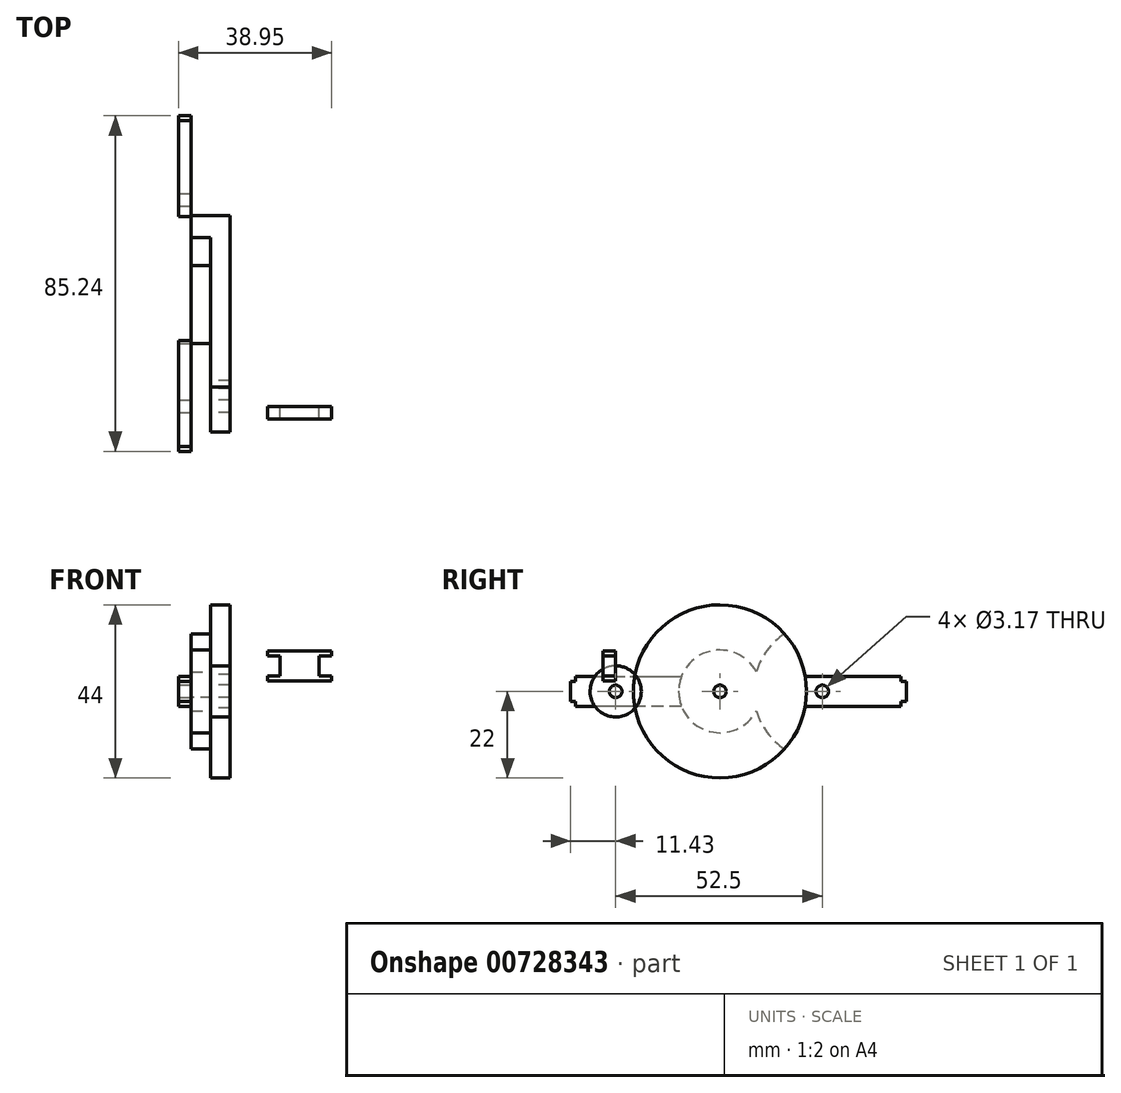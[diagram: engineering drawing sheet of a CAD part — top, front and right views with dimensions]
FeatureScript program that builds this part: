
annotation { "Feature Type Name" : "Feature", "Feature Type Description" : "" }
export const myFeature = defineFeature(function(context is Context, id is Id, definition is map)
    precondition{}
    {
        {
            var Q0;
            Q0=qCreatedBy(makeId("Right.planeOp"),FACE);
            var sketch = newSketch(context, id + "F0", { "sketchPlane" : qUnion([Q0])});
            skCircle(sketch, "E0", {"center": v(0, 0) * mm, "radius": 6.5 * mm});
            skCircle(sketch, "E1", {"center": v(0, 0) * mm, "radius": 4.5 * mm});
            skLineSegment(sketch, "E2", {"start": v(0, 0) * mm, "end": v(26.5, 0) * mm});
            skCircle(sketch, "E3", {"center": v(26.5, 0) * mm, "radius": 20 * mm});
            skCircle(sketch, "E4", {"center": v(26.5, 0) * mm, "radius": 22 * mm});
            skLineSegment(sketch, "E5.bottom", {"start": v(48.5, -25.09) * mm, "end": v(-11.83, -25.09) * mm});
            skLineSegment(sketch, "E5.top", {"start": v(48.5, 25.71) * mm, "end": v(-11.83, 25.71) * mm});
            skLineSegment(sketch, "E5.left", {"start": v(48.5, -25.09) * mm, "end": v(48.5, 25.71) * mm});
            skLineSegment(sketch, "E5.right", {"start": v(-11.83, -25.09) * mm, "end": v(-11.83, 25.71) * mm});
            skPoint(sketch, "E6", {"position": v(48.5, 0.31) * mm});
            skCircle(sketch, "E7", {"center": v(26.5, 0) * mm, "radius": 1.59 * mm});
            skCircle(sketch, "E8", {"center": v(0, 0) * mm, "radius": 1.59 * mm});
            skLineSegment(sketch, "E9.bottom", {"start": v(48.5, 25.71) * mm, "end": v(51.67, 25.71) * mm});
            skLineSegment(sketch, "E9.top", {"start": v(48.5, -25.09) * mm, "end": v(51.67, -25.09) * mm});
            skLineSegment(sketch, "E9.left", {"start": v(48.5, 25.71) * mm, "end": v(48.5, -25.09) * mm});
            skLineSegment(sketch, "E9.right", {"start": v(51.67, 25.71) * mm, "end": v(51.67, -25.09) * mm});
            skSolve(sketch);
        }
        {
            var Q0;
            Q0=makeQuery(id+"F0.imprint","IMPRINT",FACE,{"disambiguationData":[TD([[makeQuery(id+"F0.imprint","IMPRINT",EDGE,{"derivedFrom":sQuery(id+"F0.wireOp",EDGE,"E1")}),1.0]])]});
            var Q1;
            Q1=makeQuery(id+"F0.imprint","IMPRINT",FACE,{"disambiguationData":[TD([[makeQuery(id+"F0.imprint","IMPRINT",EDGE,{"derivedFrom":sQuery(id+"F0.wireOp",EDGE,"E3")}),1.0]])]});
            var Q2;
            {var subQ0=sQuery(id+"F0.wireOp",EDGE,"E4");var subQ1=sQuery(id+"F0.wireOp",EDGE,"E0");var subQ2=makeQuery(id+"F0.imprint","INTERSECT",VERTEX,{"disambiguationData":[OD(0.0)],"derivedFrom":[subQ1,subQ0]});Q2=makeQuery(id+"F0.imprint","IMPRINT",FACE,{"disambiguationData":[TD([[makeQuery(id+"F0.imprint","IMPRINT",EDGE,{"disambiguationData":[TD([[subQ2,1.0]])],"derivedFrom":subQ1}),1.0]])]});}
            var Q3;
            {var subQ1=sQuery(id+"F0.wireOp",EDGE,"E0");var subQ3=sQuery(id+"F0.wireOp",EDGE,"E4");var subQ4=makeQuery(id+"F0.imprint","INTERSECT",VERTEX,{"disambiguationData":[OD(1.0)],"derivedFrom":[subQ1,subQ3]});Q3=makeQuery(id+"F0.imprint","IMPRINT",FACE,{"disambiguationData":[TD([[makeQuery(id+"F0.imprint","IMPRINT",EDGE,{"disambiguationData":[TD([[subQ4,-1.0]])],"derivedFrom":subQ1}),1.0]])]});}
            var Q4;
            {var subQ4=sQuery(id+"F0.wireOp",EDGE,"E3");Q4=makeQuery(id+"F0.imprint","IMPRINT",FACE,{"disambiguationData":[TD([[makeQuery(id+"F0.imprint","IMPRINT",EDGE,{"derivedFrom":subQ4}),-1.0]])]});}
            var Q5;
            {var subQ4=sQuery(id+"F0.wireOp",EDGE,"E1");Q5=makeQuery(id+"F0.imprint","IMPRINT",FACE,{"disambiguationData":[TD([[makeQuery(id+"F0.imprint","IMPRINT",EDGE,{"derivedFrom":subQ4}),-1.0]])]});}
            extrude(context, id + "F1", {"entities" : qUnion([Q0, Q1, Q2, Q3, Q4, Q5]), "depth" : 5 * mm, "offsetDistance" : 25.4 * mm});
        }
        {
            var Q0;
            Q0=makeQuery(id+"F1.opExtrude","CAP_FACE",FACE,{"disambiguationData":[OSD([sQuery(id+"F0.wireOp",EDGE,"E0"),sQuery(id+"F0.wireOp",EDGE,"E4"),sQuery(id+"F0.wireOp",EDGE,"E7"),sQuery(id+"F0.wireOp",EDGE,"E8")])],"isStart":true});
            var sketch = newSketch(context, id + "F2", { "sketchPlane" : qUnion([Q0])});
            skCircle(sketch, "E10", {"center": v(-26.5, 0) * mm, "radius": 8.5 * mm});
            skCircle(sketch, "E11", {"center": v(-26.5, 0) * mm, "radius": 10.5 * mm});
            skLineSegment(sketch, "E12", {"start": v(-26.5, 0) * mm, "end": v(-52.5, 0) * mm});
            skCircle(sketch, "E13", {"center": v(-52.5, 0) * mm, "radius": 17.5 * mm});
            skCircle(sketch, "E14", {"center": v(-52.5, 0) * mm, "radius": 15.5 * mm});
            skCircle(sketch, "E15", {"center": v(-52.5, 0) * mm, "radius": 1.59 * mm});
            skSolve(sketch);
        }
        {
            var Q0;
            {var subQ1=sQuery(id+"F2.wireOp",EDGE,"E12");var subQ3=makeQuery(id+"F1.opExtrude","CAP_EDGE",EDGE,{"disambiguationData":[OSD([sQuery(id+"F0.wireOp",EDGE,"E4")])],"isStart":true});var subQ4=makeQuery(id+"F2.imprint","INTERSECT",VERTEX,{"derivedFrom":[subQ3,subQ1]});Q0=makeQuery(id+"F2.imprint","IMPRINT",FACE,{"disambiguationData":[TD([[makeQuery(id+"F2.imprint","IMPRINT",EDGE,{"disambiguationData":[TD([[subQ4,1.0]])],"derivedFrom":subQ3}),-1.0]])]});}
            var Q1;
            {var subQ1=sQuery(id+"F2.wireOp",EDGE,"E12");var subQ3=makeQuery(id+"F1.opExtrude","CAP_EDGE",EDGE,{"disambiguationData":[OSD([sQuery(id+"F0.wireOp",EDGE,"E4")])],"isStart":true});var subQ4=makeQuery(id+"F2.imprint","INTERSECT",VERTEX,{"derivedFrom":[subQ3,subQ1]});Q1=makeQuery(id+"F2.imprint","IMPRINT",FACE,{"disambiguationData":[TD([[makeQuery(id+"F2.imprint","IMPRINT",EDGE,{"disambiguationData":[TD([[subQ4,-1.0]])],"derivedFrom":subQ3}),-1.0]])]});}
            var Q2;
            {var subQ0=sQuery(id+"F2.wireOp",EDGE,"E14");var subQ1=makeQuery(id+"F1.opExtrude","CAP_EDGE",EDGE,{"disambiguationData":[OSD([sQuery(id+"F0.wireOp",EDGE,"E4")])],"isStart":true});var subQ2=makeQuery(id+"F2.imprint","INTERSECT",VERTEX,{"disambiguationData":[OD(0.0)],"derivedFrom":[subQ1,subQ0]});Q2=makeQuery(id+"F2.imprint","IMPRINT",FACE,{"disambiguationData":[TD([[makeQuery(id+"F2.imprint","IMPRINT",EDGE,{"disambiguationData":[TD([[subQ2,-1.0]])],"derivedFrom":subQ0}),1.0]])]});}
            var Q3;
            Q3=makeQuery(id+"F2.imprint","IMPRINT",FACE,{"disambiguationData":[TD([[makeQuery(id+"F2.imprint","IMPRINT",EDGE,{"derivedFrom":sQuery(id+"F2.wireOp",EDGE,"E10")}),1.0]])]});
            var Q4;
            {var subQ0=sQuery(id+"F2.wireOp",EDGE,"E13");var subQ1=sQuery(id+"F2.wireOp",EDGE,"E11");var subQ2=makeQuery(id+"F2.imprint","INTERSECT",VERTEX,{"disambiguationData":[OD(0.0)],"derivedFrom":[subQ1,subQ0]});Q4=makeQuery(id+"F2.imprint","IMPRINT",FACE,{"disambiguationData":[TD([[makeQuery(id+"F2.imprint","IMPRINT",EDGE,{"disambiguationData":[TD([[subQ2,-1.0]])],"derivedFrom":subQ1}),1.0]])]});}
            var Q5;
            {var subQ0=sQuery(id+"F2.wireOp",EDGE,"E13");var subQ1=sQuery(id+"F2.wireOp",EDGE,"E11");var subQ2=makeQuery(id+"F2.imprint","INTERSECT",VERTEX,{"disambiguationData":[OD(1.0)],"derivedFrom":[subQ1,subQ0]});Q5=makeQuery(id+"F2.imprint","IMPRINT",FACE,{"disambiguationData":[TD([[makeQuery(id+"F2.imprint","IMPRINT",EDGE,{"disambiguationData":[TD([[subQ2,1.0]])],"derivedFrom":subQ1}),1.0]])]});}
            var Q6;
            {var subQ0=sQuery(id+"F2.wireOp",EDGE,"E13");var subQ1=sQuery(id+"F2.wireOp",EDGE,"E11");var subQ2=makeQuery(id+"F2.imprint","INTERSECT",VERTEX,{"disambiguationData":[OD(1.0)],"derivedFrom":[subQ1,subQ0]});Q6=makeQuery(id+"F2.imprint","IMPRINT",FACE,{"disambiguationData":[TD([[makeQuery(id+"F2.imprint","IMPRINT",EDGE,{"disambiguationData":[TD([[subQ2,1.0]])],"derivedFrom":subQ0}),1.0]])]});}
            var Q7;
            {var subQ0=sQuery(id+"F2.wireOp",EDGE,"E10");Q7=makeQuery(id+"F2.imprint","IMPRINT",FACE,{"disambiguationData":[TD([[makeQuery(id+"F2.imprint","IMPRINT",EDGE,{"derivedFrom":subQ0}),-1.0]])]});}
            var Q8;
            {var subQ0=sQuery(id+"F2.wireOp",EDGE,"E13");var subQ1=sQuery(id+"F2.wireOp",EDGE,"E11");var subQ2=makeQuery(id+"F2.imprint","INTERSECT",VERTEX,{"disambiguationData":[OD(0.0)],"derivedFrom":[subQ1,subQ0]});Q8=makeQuery(id+"F2.imprint","IMPRINT",FACE,{"disambiguationData":[TD([[makeQuery(id+"F2.imprint","IMPRINT",EDGE,{"disambiguationData":[TD([[subQ2,-1.0]])],"derivedFrom":subQ0}),1.0]])]});}
            var Q9;
            {var subQ0=sQuery(id+"F2.wireOp",EDGE,"E13");var subQ1=makeQuery(id+"F1.opExtrude","CAP_EDGE",EDGE,{"disambiguationData":[OSD([sQuery(id+"F0.wireOp",EDGE,"E4")])],"isStart":true});var subQ2=makeQuery(id+"F2.imprint","INTERSECT",VERTEX,{"disambiguationData":[OD(0.0)],"derivedFrom":[subQ1,subQ0]});Q9=makeQuery(id+"F2.imprint","IMPRINT",FACE,{"disambiguationData":[TD([[makeQuery(id+"F2.imprint","IMPRINT",EDGE,{"disambiguationData":[TD([[subQ2,-1.0]])],"derivedFrom":subQ0}),1.0]])]});}
            extrude(context, id + "F3", {"entities" : qUnion([Q0, Q1, Q2, Q3, Q4, Q5, Q6, Q7, Q8, Q9]), "operationType" : NewBodyOperationType.ADD, "depth" : 5 * mm, "offsetDistance" : 25.4 * mm});
        }
        {
            var Q0;
            Q0=makeQuery(id+"F3.opExtrude","CAP_FACE",FACE,{"disambiguationData":[OSD([sQuery(id+"F0.wireOp",EDGE,"E7"),sQuery(id+"F2.wireOp",EDGE,"E11"),sQuery(id+"F2.wireOp",EDGE,"E13"),sQuery(id+"F2.wireOp",EDGE,"E15")])],"isStart":false});
            var sketch = newSketch(context, id + "F4", { "sketchPlane" : qUnion([Q0])});
            skCircle(sketch, "E16", {"center": v(-52.5, 0) * mm, "radius": 1.59 * mm});
            skCircle(sketch, "E17", {"center": v(-26.5, 0) * mm, "radius": 1.59 * mm});
            skLineSegment(sketch, "E18", {"start": v(-52.5, 0) * mm, "end": v(-70, 0) * mm});
            skLineSegment(sketch, "E19", {"start": v(-70, 0) * mm, "end": v(-72.54, 0) * mm});
            skLineSegment(sketch, "E20", {"start": v(-72.54, 0) * mm, "end": v(-72.54, -3.81) * mm});
            skLineSegment(sketch, "E21", {"start": v(-72.54, -3.81) * mm, "end": v(0, -3.81) * mm});
            skLineSegment(sketch, "E22", {"start": v(0, -3.81) * mm, "end": v(10.16, -3.81) * mm});
            skLineSegment(sketch, "E23", {"start": v(10.16, -3.8) * mm, "end": v(10.16, 0) * mm});
            skLineSegment(sketch, "E24", {"start": v(10.16, 0) * mm, "end": v(10.16, 3.81) * mm});
            skLineSegment(sketch, "E25", {"start": v(10.16, 3.81) * mm, "end": v(-72.54, 3.81) * mm});
            skLineSegment(sketch, "E26", {"start": v(-72.54, 3.81) * mm, "end": v(-72.54, 0) * mm});
            skLineSegment(sketch, "E27", {"start": v(-72.54, 0) * mm, "end": v(-73.8, 0) * mm});
            skLineSegment(sketch, "E28", {"start": v(-73.8, 0) * mm, "end": v(-73.8, -2.54) * mm});
            skLineSegment(sketch, "E29", {"start": v(-73.8, -2.54) * mm, "end": v(-72.54, -2.54) * mm});
            skLineSegment(sketch, "E30.MirrorCS", {"start": v(-73.8, 0) * mm, "end": v(-73.8, 2.54) * mm});
            skLineSegment(sketch, "E31.MirrorCS", {"start": v(-73.8, 2.54) * mm, "end": v(-72.54, 2.54) * mm});
            skLineSegment(sketch, "E32", {"start": v(10.16, 0) * mm, "end": v(11.43, 0) * mm});
            skLineSegment(sketch, "E33", {"start": v(11.43, 0) * mm, "end": v(11.43, -2.54) * mm});
            skLineSegment(sketch, "E34", {"start": v(11.43, -2.54) * mm, "end": v(10.16, -2.54) * mm});
            skLineSegment(sketch, "E35.MirrorCS", {"start": v(11.43, 0) * mm, "end": v(11.43, 2.54) * mm});
            skLineSegment(sketch, "E36.MirrorCS", {"start": v(11.43, 2.54) * mm, "end": v(10.16, 2.54) * mm});
            skCircle(sketch, "E37", {"center": v(0, 0) * mm, "radius": 1.59 * mm});
            skSolve(sketch);
        }
        {
            var Q0;
            Q0=makeQuery(id+"F4.imprint","IMPRINT",FACE,{"disambiguationData":[TD([[makeQuery(id+"F4.imprint","IMPRINT",EDGE,{"derivedFrom":sQuery(id+"F4.wireOp",EDGE,"E16")}),-1.0]])]});
            var Q1;
            {var subQ6=sQuery(id+"F4.wireOp",EDGE,"E19");Q1=makeQuery(id+"F4.imprint","IMPRINT",FACE,{"disambiguationData":[TD([[makeQuery(id+"F4.imprint","IMPRINT",EDGE,{"derivedFrom":subQ6}),-1.0]])]});}
            var Q2;
            {var subQ6=sQuery(id+"F4.wireOp",EDGE,"E19");Q2=makeQuery(id+"F4.imprint","IMPRINT",FACE,{"disambiguationData":[TD([[makeQuery(id+"F4.imprint","IMPRINT",EDGE,{"derivedFrom":subQ6}),1.0]])]});}
            var Q3;
            {var subQ0=sQuery(id+"F4.wireOp",EDGE,"E27");Q3=makeQuery(id+"F4.imprint","IMPRINT",FACE,{"disambiguationData":[TD([[makeQuery(id+"F4.imprint","IMPRINT",EDGE,{"derivedFrom":subQ0}),1.0]])]});}
            var Q4;
            {var subQ0=sQuery(id+"F4.wireOp",EDGE,"E27");Q4=makeQuery(id+"F4.imprint","IMPRINT",FACE,{"disambiguationData":[TD([[makeQuery(id+"F4.imprint","IMPRINT",EDGE,{"derivedFrom":subQ0}),-1.0]])]});}
            var Q5;
            {var subQ4=sQuery(id+"F4.wireOp",EDGE,"E22");Q5=makeQuery(id+"F4.imprint","IMPRINT",FACE,{"disambiguationData":[TD([[makeQuery(id+"F4.imprint","IMPRINT",EDGE,{"derivedFrom":subQ4}),1.0]])]});}
            var Q6;
            {var subQ0=sQuery(id+"F4.wireOp",EDGE,"E32");Q6=makeQuery(id+"F4.imprint","IMPRINT",FACE,{"disambiguationData":[TD([[makeQuery(id+"F4.imprint","IMPRINT",EDGE,{"derivedFrom":subQ0}),1.0]])]});}
            var Q7;
            {var subQ0=sQuery(id+"F4.wireOp",EDGE,"E32");Q7=makeQuery(id+"F4.imprint","IMPRINT",FACE,{"disambiguationData":[TD([[makeQuery(id+"F4.imprint","IMPRINT",EDGE,{"derivedFrom":subQ0}),-1.0]])]});}
            extrude(context, id + "F5", {"entities" : qUnion([Q0, Q1, Q2, Q3, Q4, Q5, Q6, Q7]), "depth" : 3.17 * mm, "offsetDistance" : 25.4 * mm});
        }
        {
            var Q0;
            Q0=qCreatedBy(makeId("Front.planeOp"),FACE);
            var sketch = newSketch(context, id + "F6", { "sketchPlane" : qUnion([Q0])});
            skLineSegment(sketch, "E38.bottom", {"start": v(30.77, 10.22) * mm, "end": v(14.42, 10.22) * mm});
            skLineSegment(sketch, "E38.top", {"start": v(30.77, 2.6) * mm, "end": v(14.42, 2.6) * mm});
            skLineSegment(sketch, "E38.left", {"start": v(30.77, 10.22) * mm, "end": v(30.77, 2.6) * mm});
            skLineSegment(sketch, "E38.right", {"start": v(14.42, 10.22) * mm, "end": v(14.42, 2.6) * mm});
            skLineSegment(sketch, "E39", {"start": v(30.77, 10.22) * mm, "end": v(30.77, 8.95) * mm});
            skLineSegment(sketch, "E40", {"start": v(30.77, 8.95) * mm, "end": v(27.6, 8.95) * mm});
            skLineSegment(sketch, "E41", {"start": v(27.6, 8.95) * mm, "end": v(27.6, 3.87) * mm});
            skLineSegment(sketch, "E42", {"start": v(27.6, 3.87) * mm, "end": v(30.77, 3.87) * mm});
            skLineSegment(sketch, "E43", {"start": v(22.6, 10.22) * mm, "end": v(22.6, 2.6) * mm});
            skLineSegment(sketch, "E44.MirrorCS", {"start": v(17.6, 8.95) * mm, "end": v(17.6, 3.87) * mm});
            skLineSegment(sketch, "E45.MirrorCS", {"start": v(17.6, 3.87) * mm, "end": v(14.42, 3.87) * mm});
            skLineSegment(sketch, "E46.MirrorCS", {"start": v(14.42, 8.95) * mm, "end": v(17.6, 8.95) * mm});
            skSolve(sketch);
        }
        {
            var Q0;
            {var subQ0=sQuery(id+"F6.wireOp",EDGE,"E40");Q0=makeQuery(id+"F6.imprint","IMPRINT",FACE,{"disambiguationData":[TD([[makeQuery(id+"F6.imprint","IMPRINT",EDGE,{"derivedFrom":subQ0}),-1.0]])]});}
            var Q1;
            {var subQ7=sQuery(id+"F6.wireOp",EDGE,"E43");Q1=makeQuery(id+"F6.imprint","IMPRINT",FACE,{"disambiguationData":[TD([[makeQuery(id+"F6.imprint","IMPRINT",EDGE,{"derivedFrom":subQ7}),-1.0]])]});}
            extrude(context, id + "F7", {"entities" : qUnion([Q0, Q1]), "depth" : 3.17 * mm, "offsetDistance" : 25.4 * mm});
        }
    });
